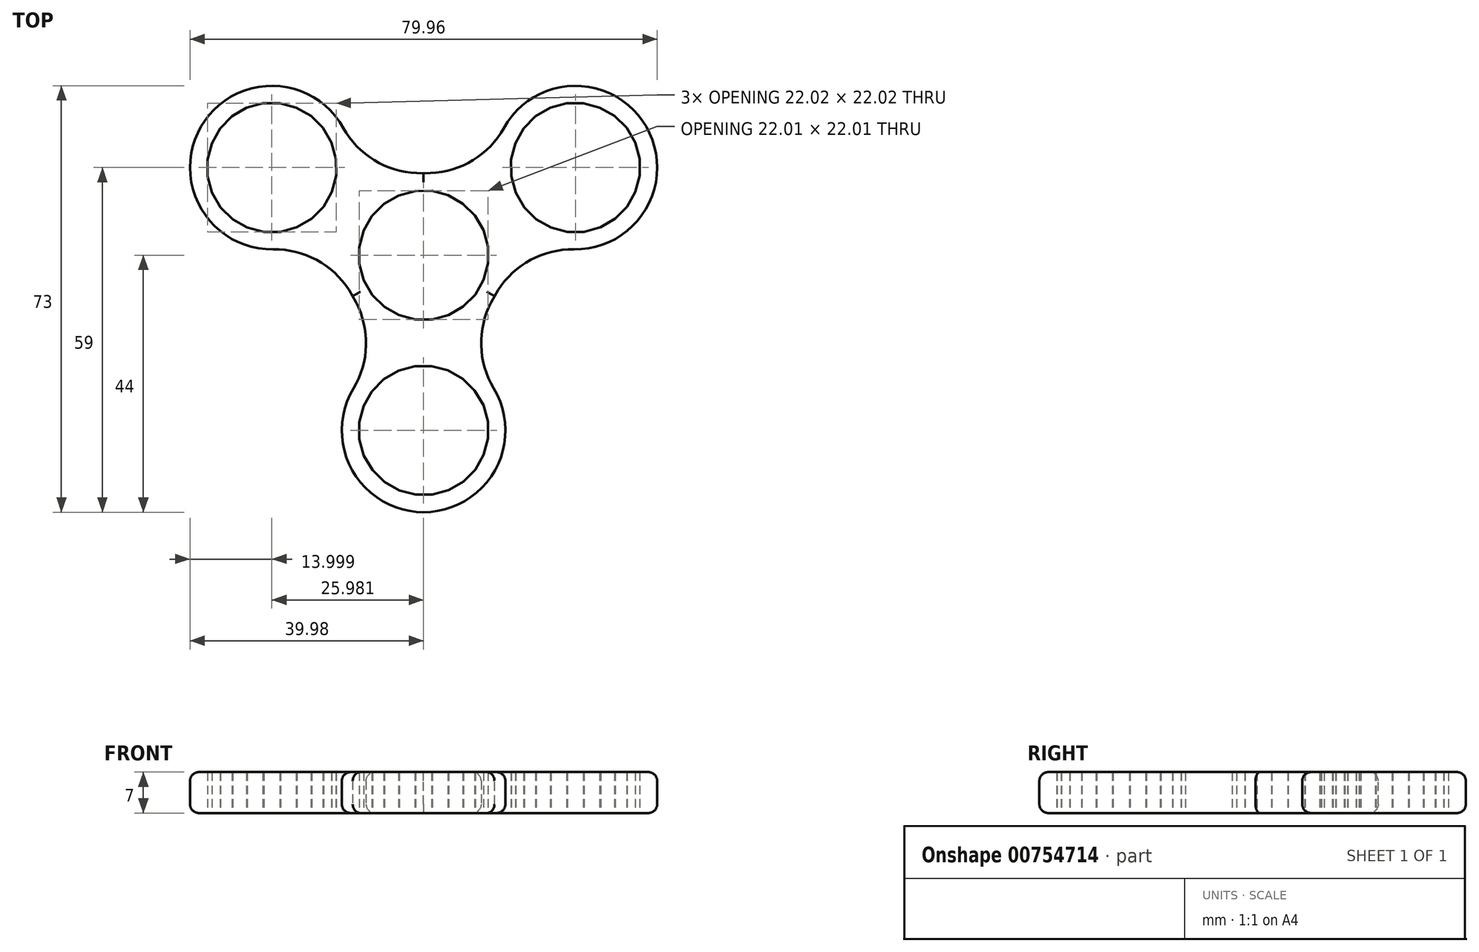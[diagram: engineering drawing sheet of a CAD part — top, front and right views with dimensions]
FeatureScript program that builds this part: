
annotation { "Feature Type Name" : "Feature", "Feature Type Description" : "" }
export const myFeature = defineFeature(function(context is Context, id is Id, definition is map)
    precondition{}
    {
        {
            var Q0;
            Q0=qCreatedBy(makeId("Front.planeOp"),FACE);
            var sketch = newSketch(context, id + "F0", { "sketchPlane" : qUnion([Q0])});
            skLineSegment(sketch, "E0", {"start": v(0, 0) * mm, "end": v(0, 6.84) * mm, "construction": true});
            skSolve(sketch);
        }
        {
            var Q0;
            Q0=qCreatedBy(makeId("Top.planeOp"),FACE);
            var sketch = newSketch(context, id + "F1", { "sketchPlane" : qUnion([Q0])});
            skCircle(sketch, "E1", {"center": v(0, 0) * mm, "radius": 14 * mm});
            skCircle(sketch, "E2", {"center": v(0, -30) * mm, "radius": 14 * mm});
            skLineSegment(sketch, "E3", {"start": v(0, 0) * mm, "end": v(0, -30) * mm, "construction": true});
            skCircle(sketch, "E4.cCircle", {"center": v(0, -30) * mm, "radius": 11 * mm, "construction": true});
            skLineSegment(sketch, "E4.0", {"start": v(-8.84, -23.3) * mm, "end": v(-6.8, -21.24) * mm});
            skLineSegment(sketch, "E4.1", {"start": v(-6.8, -21.24) * mm, "end": v(-4.3, -19.78) * mm});
            skLineSegment(sketch, "E4.2", {"start": v(-4.3, -19.78) * mm, "end": v(-1.52, -19) * mm});
            skLineSegment(sketch, "E4.3", {"start": v(-1.52, -19) * mm, "end": v(1.38, -19) * mm});
            skLineSegment(sketch, "E4.4", {"start": v(1.38, -19) * mm, "end": v(4.18, -19.72) * mm});
            skLineSegment(sketch, "E4.5", {"start": v(4.18, -19.72) * mm, "end": v(6.7, -21.16) * mm});
            skLineSegment(sketch, "E4.6", {"start": v(6.7, -21.16) * mm, "end": v(8.76, -23.2) * mm});
            skLineSegment(sketch, "E4.7", {"start": v(8.76, -23.2) * mm, "end": v(10.22, -25.7) * mm});
            skLineSegment(sketch, "E4.8", {"start": v(10.22, -25.7) * mm, "end": v(11, -28.48) * mm});
            skLineSegment(sketch, "E4.9", {"start": v(11, -28.48) * mm, "end": v(11, -31.38) * mm});
            skLineSegment(sketch, "E4.10", {"start": v(11, -31.38) * mm, "end": v(10.28, -34.18) * mm});
            skLineSegment(sketch, "E4.11", {"start": v(10.28, -34.18) * mm, "end": v(8.84, -36.7) * mm});
            skLineSegment(sketch, "E4.12", {"start": v(8.84, -36.7) * mm, "end": v(6.8, -38.76) * mm});
            skLineSegment(sketch, "E4.13", {"start": v(6.8, -38.76) * mm, "end": v(4.3, -40.22) * mm});
            skLineSegment(sketch, "E4.14", {"start": v(4.3, -40.22) * mm, "end": v(1.52, -41) * mm});
            skLineSegment(sketch, "E4.15", {"start": v(1.52, -41) * mm, "end": v(-1.38, -41) * mm});
            skLineSegment(sketch, "E4.16", {"start": v(-1.38, -41) * mm, "end": v(-4.18, -40.28) * mm});
            skLineSegment(sketch, "E4.17", {"start": v(-4.18, -40.28) * mm, "end": v(-6.7, -38.84) * mm});
            skLineSegment(sketch, "E4.18", {"start": v(-6.7, -38.84) * mm, "end": v(-8.76, -36.8) * mm});
            skLineSegment(sketch, "E4.19", {"start": v(-8.76, -36.8) * mm, "end": v(-10.22, -34.3) * mm});
            skLineSegment(sketch, "E4.20", {"start": v(-10.22, -34.3) * mm, "end": v(-11, -31.52) * mm});
            skLineSegment(sketch, "E4.21", {"start": v(-11, -31.52) * mm, "end": v(-11, -28.62) * mm});
            skLineSegment(sketch, "E4.22", {"start": v(-11, -28.62) * mm, "end": v(-10.28, -25.82) * mm});
            skLineSegment(sketch, "E4.23", {"start": v(-10.28, -25.82) * mm, "end": v(-8.84, -23.3) * mm});
            skPoint(sketch, "E4.0.midPoint", {"position": v(-7.83, -22.27) * mm});
            skCircle(sketch, "E5.cCircle", {"center": v(0, 0) * mm, "radius": 11 * mm, "construction": true});
            skLineSegment(sketch, "E5.0", {"start": v(10.27, -4.2) * mm, "end": v(8.83, -6.72) * mm});
            skLineSegment(sketch, "E5.1", {"start": v(8.83, -6.72) * mm, "end": v(6.79, -8.78) * mm});
            skLineSegment(sketch, "E5.2", {"start": v(6.79, -8.78) * mm, "end": v(4.28, -10.23) * mm});
            skLineSegment(sketch, "E5.3", {"start": v(4.28, -10.23) * mm, "end": v(1.49, -11) * mm});
            skLineSegment(sketch, "E5.4", {"start": v(1.49, -11) * mm, "end": v(-1.4, -11) * mm});
            skLineSegment(sketch, "E5.5", {"start": v(-1.4, -11) * mm, "end": v(-4.2, -10.27) * mm});
            skLineSegment(sketch, "E5.6", {"start": v(-4.2, -10.27) * mm, "end": v(-6.72, -8.83) * mm});
            skLineSegment(sketch, "E5.7", {"start": v(-6.72, -8.83) * mm, "end": v(-8.78, -6.79) * mm});
            skLineSegment(sketch, "E5.8", {"start": v(-8.78, -6.79) * mm, "end": v(-10.23, -4.28) * mm});
            skLineSegment(sketch, "E5.9", {"start": v(-10.23, -4.28) * mm, "end": v(-11, -1.49) * mm});
            skLineSegment(sketch, "E5.10", {"start": v(-11, -1.49) * mm, "end": v(-11, 1.4) * mm});
            skLineSegment(sketch, "E5.11", {"start": v(-11, 1.4) * mm, "end": v(-10.27, 4.2) * mm});
            skLineSegment(sketch, "E5.12", {"start": v(-10.27, 4.2) * mm, "end": v(-8.83, 6.72) * mm});
            skLineSegment(sketch, "E5.13", {"start": v(-8.83, 6.72) * mm, "end": v(-6.79, 8.78) * mm});
            skLineSegment(sketch, "E5.14", {"start": v(-6.79, 8.78) * mm, "end": v(-4.28, 10.23) * mm});
            skLineSegment(sketch, "E5.15", {"start": v(-4.28, 10.23) * mm, "end": v(-1.49, 11) * mm});
            skLineSegment(sketch, "E5.16", {"start": v(-1.49, 11) * mm, "end": v(1.4, 11) * mm});
            skLineSegment(sketch, "E5.17", {"start": v(1.4, 11) * mm, "end": v(4.2, 10.27) * mm});
            skLineSegment(sketch, "E5.18", {"start": v(4.2, 10.27) * mm, "end": v(6.72, 8.83) * mm});
            skLineSegment(sketch, "E5.19", {"start": v(6.72, 8.83) * mm, "end": v(8.78, 6.79) * mm});
            skLineSegment(sketch, "E5.20", {"start": v(8.78, 6.79) * mm, "end": v(10.23, 4.28) * mm});
            skLineSegment(sketch, "E5.21", {"start": v(10.23, 4.28) * mm, "end": v(11, 1.49) * mm});
            skLineSegment(sketch, "E5.22", {"start": v(11, 1.49) * mm, "end": v(11, -1.4) * mm});
            skLineSegment(sketch, "E5.23", {"start": v(11, -1.4) * mm, "end": v(10.27, -4.2) * mm});
            skPoint(sketch, "E5.0.midPoint", {"position": v(9.55, -5.46) * mm});
            skLineSegment(sketch, "E6", {"start": v(0, -30) * mm, "end": v(12.38, -6.53) * mm});
            skLineSegment(sketch, "E7.MirrorCS", {"start": v(0, -30) * mm, "end": v(-12.38, -6.53) * mm});
            skSolve(sketch);
        }
        {
            var Q0;
            Q0 = qSketchRegion(id + "F1", true);
            extrude(context, id + "F2", {"entities" : qUnion([Q0]), "depth" : 7 * mm, "offsetDistance" : 25 * mm});
        }
        {
            var Q0;
            Q0=makeQuery(id+"F2.opExtrude","SWEPT_EDGE",EDGE,{"disambiguationData":[OSD([sQuery(id+"F1.wireOp",EDGE,"E2"),sQuery(id+"F1.wireOp",EDGE,"E6")])]});
            var Q1;
            Q1=makeQuery(id+"F2.opExtrude","SWEPT_EDGE",EDGE,{"disambiguationData":[OSD([sQuery(id+"F1.wireOp",EDGE,"E2"),sQuery(id+"F1.wireOp",EDGE,"E7.MirrorCS")])]});
            fillet(context, id + "F3", {"entities" : qUnion([Q0, Q1]), "radius" : 15 * mm, "tangentPropagation" : true, "allowEdgeOverflow" : false});
        }
        {
            var Q0;
            Q0=makeQuery(id+"F2.opExtrude","CAP_EDGE",EDGE,{"disambiguationData":[OSD([sQuery(id+"F1.wireOp",EDGE,"E2")])],"isStart":false});
            var Q1;
            Q1=makeQuery(id+"F2.opExtrude","CAP_EDGE",EDGE,{"disambiguationData":[OSD([sQuery(id+"F1.wireOp",EDGE,"E6")])],"isStart":false});
            var Q2;
            Q2=makeQuery(id+"F2.opExtrude","CAP_EDGE",EDGE,{"disambiguationData":[OSD([sQuery(id+"F1.wireOp",EDGE,"E6")])],"isStart":true});
            var Q3;
            Q3=makeQuery(id+"F2.opExtrude","CAP_EDGE",EDGE,{"disambiguationData":[OSD([sQuery(id+"F1.wireOp",EDGE,"E2")])],"isStart":true});
            fillet(context, id + "F4", {"entities" : qUnion([Q0, Q1, Q2, Q3]), "radius" : 1.5 * mm, "tangentPropagation" : true, "allowEdgeOverflow" : false});
        }
        {
            var Q0;
            Q0=makeQuery(id+"F2.opExtrude","SWEPT_BODY",BODY,{"disambiguationData":[OSD([sQuery(id+"F1.wireOp",EDGE,"E1"),sQuery(id+"F1.wireOp",EDGE,"E2"),sQuery(id+"F1.wireOp",EDGE,"E4.0"),sQuery(id+"F1.wireOp",EDGE,"E4.1"),sQuery(id+"F1.wireOp",EDGE,"E4.2"),sQuery(id+"F1.wireOp",EDGE,"E4.3"),sQuery(id+"F1.wireOp",EDGE,"E4.4"),sQuery(id+"F1.wireOp",EDGE,"E4.5"),sQuery(id+"F1.wireOp",EDGE,"E4.6"),sQuery(id+"F1.wireOp",EDGE,"E4.7"),sQuery(id+"F1.wireOp",EDGE,"E4.8"),sQuery(id+"F1.wireOp",EDGE,"E4.9"),sQuery(id+"F1.wireOp",EDGE,"E4.10"),sQuery(id+"F1.wireOp",EDGE,"E4.11"),sQuery(id+"F1.wireOp",EDGE,"E4.12"),sQuery(id+"F1.wireOp",EDGE,"E4.13"),sQuery(id+"F1.wireOp",EDGE,"E4.14"),sQuery(id+"F1.wireOp",EDGE,"E4.15"),sQuery(id+"F1.wireOp",EDGE,"E4.16"),sQuery(id+"F1.wireOp",EDGE,"E4.17"),sQuery(id+"F1.wireOp",EDGE,"E4.18"),sQuery(id+"F1.wireOp",EDGE,"E4.19"),sQuery(id+"F1.wireOp",EDGE,"E4.20"),sQuery(id+"F1.wireOp",EDGE,"E4.21"),sQuery(id+"F1.wireOp",EDGE,"E4.22"),sQuery(id+"F1.wireOp",EDGE,"E4.23"),sQuery(id+"F1.wireOp",EDGE,"E5.0"),sQuery(id+"F1.wireOp",EDGE,"E5.1"),sQuery(id+"F1.wireOp",EDGE,"E5.2"),sQuery(id+"F1.wireOp",EDGE,"E5.3"),sQuery(id+"F1.wireOp",EDGE,"E5.4"),sQuery(id+"F1.wireOp",EDGE,"E5.5"),sQuery(id+"F1.wireOp",EDGE,"E5.6"),sQuery(id+"F1.wireOp",EDGE,"E5.7"),sQuery(id+"F1.wireOp",EDGE,"E5.8"),sQuery(id+"F1.wireOp",EDGE,"E5.9"),sQuery(id+"F1.wireOp",EDGE,"E5.10"),sQuery(id+"F1.wireOp",EDGE,"E5.11"),sQuery(id+"F1.wireOp",EDGE,"E5.12"),sQuery(id+"F1.wireOp",EDGE,"E5.13"),sQuery(id+"F1.wireOp",EDGE,"E5.14"),sQuery(id+"F1.wireOp",EDGE,"E5.15"),sQuery(id+"F1.wireOp",EDGE,"E5.16"),sQuery(id+"F1.wireOp",EDGE,"E5.17"),sQuery(id+"F1.wireOp",EDGE,"E5.18"),sQuery(id+"F1.wireOp",EDGE,"E5.19"),sQuery(id+"F1.wireOp",EDGE,"E5.20"),sQuery(id+"F1.wireOp",EDGE,"E5.21"),sQuery(id+"F1.wireOp",EDGE,"E5.22"),sQuery(id+"F1.wireOp",EDGE,"E5.23"),sQuery(id+"F1.wireOp",EDGE,"E6"),sQuery(id+"F1.wireOp",EDGE,"E7.MirrorCS")])]});
            var Q1;
            Q1=sQuery(id+"F0.wireOp",EDGE,"E0");
            circularPattern(context, id + "F5", {"operationType" : NewBodyOperationType.ADD, "entities" : qUnion([Q0]), "axis" : qUnion([Q1]), "angle" : 360 * degree, "instanceCount" : 3, "equalSpace" : true});
        }
    });
